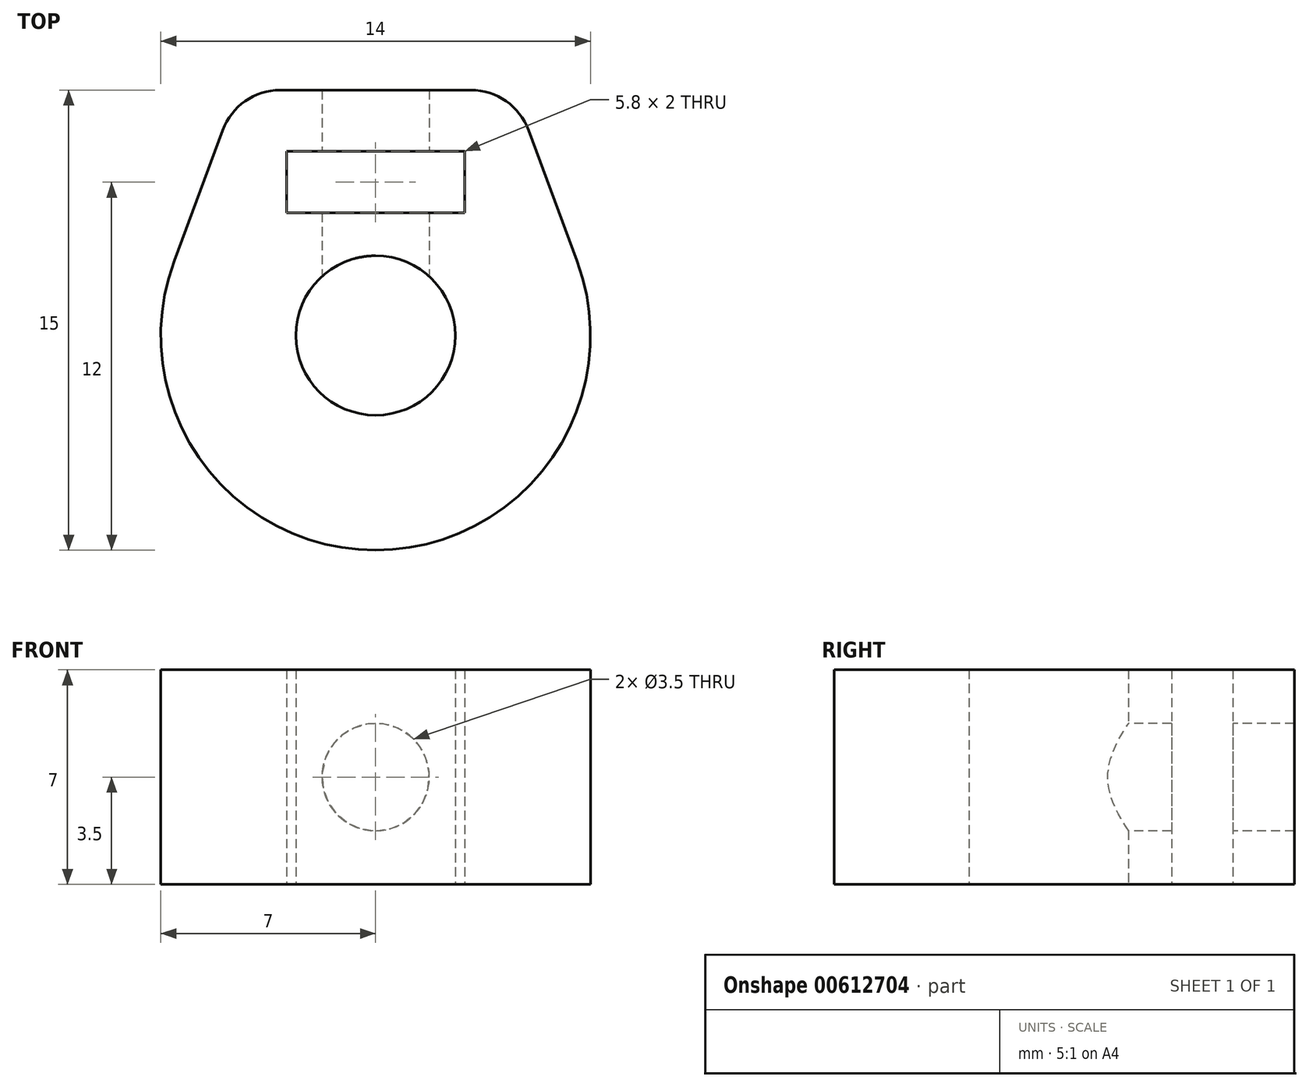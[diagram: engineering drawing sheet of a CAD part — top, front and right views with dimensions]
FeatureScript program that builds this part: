
annotation { "Feature Type Name" : "Feature", "Feature Type Description" : "" }
export const myFeature = defineFeature(function(context is Context, id is Id, definition is map)
    precondition{}
    {
        {
            var Q0;
            Q0=qCreatedBy(makeId("Top.planeOp"),FACE);
            var sketch = newSketch(context, id + "F0", { "sketchPlane" : qUnion([Q0])});
            skCircle(sketch, "E0", {"center": v(0, 0) * mm, "radius": 2.6 * mm});
            skLineSegment(sketch, "E1", {"start": v(-6.56, 2.43) * mm, "end": v(-4.5, 8) * mm});
            skLineSegment(sketch, "E2", {"start": v(-4.5, 8) * mm, "end": v(4.5, 8) * mm});
            skLineSegment(sketch, "E3", {"start": v(4.5, 8) * mm, "end": v(6.56, 2.43) * mm});
            skArc(sketch, "E4", {"start": v(-6.56, 2.43) * mm, "mid": v(0, -7) * mm, "end": v(6.56, 2.43) * mm});
            skLineSegment(sketch, "E5", {"start": v(-6.56, 2.43) * mm, "end": v(0, 0) * mm, "construction": true});
            skLineSegment(sketch, "E6", {"start": v(0, 0) * mm, "end": v(6.56, 2.43) * mm, "construction": true});
            skLineSegment(sketch, "E7.bottom", {"start": v(-2.9, 6) * mm, "end": v(2.9, 6) * mm});
            skLineSegment(sketch, "E7.top", {"start": v(-2.9, 4) * mm, "end": v(2.9, 4) * mm});
            skLineSegment(sketch, "E7.left", {"start": v(-2.9, 6) * mm, "end": v(-2.9, 4) * mm});
            skLineSegment(sketch, "E7.right", {"start": v(2.9, 6) * mm, "end": v(2.9, 4) * mm});
            skLineSegment(sketch, "E8", {"start": v(-2.9, 4) * mm, "end": v(0, 0) * mm, "construction": true});
            skLineSegment(sketch, "E9", {"start": v(2.9, 4) * mm, "end": v(0, 0) * mm, "construction": true});
            skSolve(sketch);
        }
        {
            var Q0;
            Q0=makeQuery(id+"F0.imprint","IMPRINT",FACE,{"disambiguationData":[TD([[makeQuery(id+"F0.imprint","IMPRINT",EDGE,{"derivedFrom":sQuery(id+"F0.wireOp",EDGE,"E0")}),-1.0]])]});
            extrude(context, id + "F1", {"entities" : qUnion([Q0]), "depth" : 7 * mm, "offsetDistance" : 25 * mm});
        }
        {
            var Q0;
            Q0=qCreatedBy(makeId("Front.planeOp"),FACE);
            cPlane(context, id + "F2", {"entities" : qUnion([Q0]), "cplaneType" : CPlaneType.OFFSET, "offset" : 1 * mm, "oppositeDirection" : true, "width" : 150 * mm, "height" : 150 * mm});
        }
        {
            var Q0;
            Q0=qCreatedBy(id+"F2.planeOp",FACE);
            var sketch = newSketch(context, id + "F3", { "sketchPlane" : qUnion([Q0])});
            skCircle(sketch, "E10", {"center": v(0, 3.5) * mm, "radius": 1.75 * mm});
            skLineSegment(sketch, "E11", {"start": v(0, 3.5) * mm, "end": v(0, 0) * mm, "construction": true});
            skSolve(sketch);
        }
        {
            var Q0;
            Q0=makeQuery(id+"F3.imprint","IMPRINT",FACE,{"disambiguationData":[TD([[makeQuery(id+"F3.imprint","IMPRINT",EDGE,{"derivedFrom":sQuery(id+"F3.wireOp",EDGE,"E10")}),1.0]])]});
            var Q1;
            Q1=makeQuery(id+"F1.opExtrude","SWEPT_FACE",FACE,{"disambiguationData":[OSD([sQuery(id+"F0.wireOp",EDGE,"Rat4CECl-X8ID-fuQZ-zJzg-11iDNskEnhmI")])]});
            extrude(context, id + "F4", {"entities" : qUnion([Q0]), "operationType" : NewBodyOperationType.REMOVE, "oppositeDirection" : true, "endBoundEntityFace" : qUnion([Q1]), "depth" : 25 * mm, "offsetDistance" : 25 * mm});
        }
        {
            var Q0;
            Q0=makeQuery(id+"F1.opExtrude","SWEPT_EDGE",EDGE,{"disambiguationData":[OSD([sQuery(id+"F0.wireOp",EDGE,"E1"),sQuery(id+"F0.wireOp",EDGE,"E2")])]});
            var Q1;
            Q1=makeQuery(id+"F1.opExtrude","SWEPT_EDGE",EDGE,{"disambiguationData":[OSD([sQuery(id+"F0.wireOp",EDGE,"E2"),sQuery(id+"F0.wireOp",EDGE,"E3")])]});
            fillet(context, id + "F5", {"entities" : qUnion([Q0, Q1]), "radius" : 2 * mm, "tangentPropagation" : true, "allowEdgeOverflow" : false});
        }
    });
